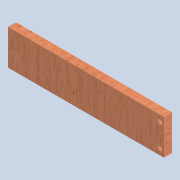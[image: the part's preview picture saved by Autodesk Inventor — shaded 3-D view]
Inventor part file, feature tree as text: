
AUTODESK INVENTOR PART (.ipt)
format: ipt  version: 2020 (Build 240168000, 168)  size: 114,176 bytes
history: native  units: mm
features: hole x2, sketch x2, extrude x1
ambient origin geometry x8: Origin, YZ Plane, XZ Plane, XY Plane, X Axis, Y Axis, Z Axis, Center Point
bodies: Solid1 (feature_tree)
feature tree (5):
  extrude  "Extrusion1"  Depth=35.0mm
  hole  "Hole1"  [1 undecoded]
  hole  "Hole2"  [1 undecoded]
  sketch  "Sketch1"  dims[d0=155.0mm d1=35.0mm]
  sketch  "Sketch4"  dims[d2=8.0mm d3=0.0mm d19=4.0mm d20=6.0mm d21=4.5mm d22=6.0mm d23=4.0mm d24=2.0mm d25=90.0deg d26=8.0mm d27=20.594885mm d28=4.0mm d29=6.0mm d30=4.0mm d31=2.0mm d32=90.0deg d33=8.0mm d34=20.594885mm]
note: 2 required parameter values undecoded (feature->parameter linkage not recoverable at this tier; creation-order binding heuristic only, values carry confidence <= 0.55)
